FCSTD DOCUMENT  (FreeCAD 1.0R39109 (Git))
Label: SD7037 Airfoil Wing w Struts
License: All rights reserved
LicenseURL: https://en.wikipedia.org/wiki/All_rights_reserved
objects: Part::Part2DObjectPython×3, App::DocumentObjectGroup×1, Sketcher::SketchObject×1
note: 5 computed .brp shape members not serialized (recipe doc carries the construction recipe); baked Part::Feature solids carry a one-line shape summary decoded from their .brp

FEATURE [Part::Part2DObjectPython] Wire  # Draft 2D object (typed FeaturePython)
  Area = 0.0605284
  ChamferSize = 0
  Closed = true
  End = (1,0,0)
  FilletRadius = 0
  Length = 2.02979
  MakeFace = true
  Points = (61) [(1,0,0),(0.99672,0.00042,0),(0.98707,0.0018,0),(0.97146,0.00436,0),(0.95041,0.00811,0),(0.9245,0.01295,0),(0.89425,0.01865,0),(0.86015,0.0249,0),+53 more]
  Start = (1,0,0)
  Subdivisions = 0
FEATURE [App::DocumentObjectGroup] sd7037
  Group = -> [Wire]
FEATURE [Part::Part2DObjectPython] BSpline  # Draft 2D object (typed FeaturePython)
  Area = 0.0607194
  Closed = true
  MakeFace = true
  Parameterization = 1
  Points = (60) [(1,0,0),(0.99672,0.00042,0),(0.98707,0.0018,0),(0.97146,0.00436,0),(0.95041,0.00811,0),(0.9245,0.01295,0),(0.89425,0.01865,0),(0.86015,0.0249,0),+52 more]
FEATURE [Part::Part2DObjectPython] Wire001  # Draft 2D object (typed FeaturePython)
  Area = 0.0605284
  ChamferSize = 0
  Closed = true
  End = (0.99671,0.00021,0)
  FilletRadius = 0
  Length = 2.02979
  MakeFace = true
  Points = (60) [(1,0,0),(0.99672,0.00042,0),(0.98707,0.0018,0),(0.97146,0.00436,0),(0.95041,0.00811,0),(0.9245,0.01295,0),(0.89425,0.01865,0),(0.86015,0.0249,0),+52 more]
  Start = (1,0,0)
  Subdivisions = 0
FEATURE [Sketcher::SketchObject] Sketch
  ArcFitTolerance = 1e-06
  FullyConstrained = false
  MakeInternals = false
  sketch-geometry (210):
    g0: BSplineCurve PolesCount=61 KnotsCount=61 Degree=3 IsPeriodic=1
    g1-g61: Circle [constr] x61 (B-spline internal-alignment scaffolding for g0; pole/knot coordinates omitted)
    g62-g122: GeomPoint [constr] x61 (B-spline internal-alignment scaffolding for g0; pole/knot coordinates omitted)
    g123: LineSegment StartX=0.00694907 StartY=0.00753743 StartZ=0 EndX=0.0125619 EndY=0.0134873 EndZ=0
    g124: LineSegment StartX=0.0125619 StartY=0.0134873 StartZ=0 EndX=0.0195813 EndY=0.0193542 EndZ=0
    g125: LineSegment StartX=0.0195813 StartY=0.0193542 StartZ=0 EndX=0.0310295 EndY=0.0261498 EndZ=0
    g126: LineSegment StartX=0.0310295 StartY=0.0261498 StartZ=0 EndX=0.046426 EndY=0.033489 EndZ=0
    g127: LineSegment StartX=0.046426 StartY=0.033489 StartZ=0 EndX=0.063433 EndY=0.039816 EndZ=0
    g128: LineSegment StartX=0.063433 StartY=0.039816 StartZ=0 EndX=0.076674 EndY=0.044075 EndZ=0
    g129: LineSegment StartX=0.076674 StartY=0.044075 StartZ=0 EndX=0.093252 EndY=0.048694 EndZ=0
    g130: LineSegment StartX=0.093252 StartY=0.048694 StartZ=0 EndX=0.121289 EndY=0.055066 EndZ=0
    g131: LineSegment StartX=0.121289 StartY=0.055066 StartZ=0 EndX=0.15085 EndY=0.059941 EndZ=0
    g132: LineSegment StartX=0.15085 StartY=0.059941 StartZ=0 EndX=0.187176 EndY=0.064723 EndZ=0
    g133: LineSegment StartX=0.187176 StartY=0.064723 StartZ=0 EndX=0.221818 EndY=0.06734 EndZ=0
    g134: LineSegment StartX=0.221818 StartY=0.06734 StartZ=0 EndX=0.262808 EndY=0.069398 EndZ=0
    g135: LineSegment StartX=0.262808 StartY=0.069398 StartZ=0 EndX=0.305939 EndY=0.071198 EndZ=0
    g136: LineSegment StartX=0.305939 StartY=0.071198 StartZ=0 EndX=0.351804 EndY=0.071413 EndZ=0
    g137: LineSegment StartX=0.351804 StartY=0.071413 StartZ=0 EndX=0.399304 EndY=0.07049 EndZ=0
    g138: LineSegment StartX=0.399304 StartY=0.07049 StartZ=0 EndX=0.447775 EndY=0.068433 EndZ=0
    g139: LineSegment StartX=0.447775 StartY=0.068433 StartZ=0 EndX=0.497089 EndY=0.065532 EndZ=0
    g140: LineSegment StartX=0.497089 StartY=0.065532 StartZ=0 EndX=0.546658 EndY=0.061579 EndZ=0
    g141: LineSegment StartX=0.546658 StartY=0.061579 StartZ=0 EndX=0.596216 EndY=0.057292 EndZ=0
    g142: LineSegment StartX=0.596216 StartY=0.057292 StartZ=0 EndX=0.644863 EndY=0.0522 EndZ=0
    g143: LineSegment StartX=0.644863 StartY=0.0522 StartZ=0 EndX=0.692328 EndY=0.046604 EndZ=0
    g144: LineSegment StartX=0.692328 StartY=0.046604 StartZ=0 EndX=0.737563 EndY=0.040632 EndZ=0
    g145: LineSegment StartX=0.737563 StartY=0.040632 StartZ=0 EndX=0.781012 EndY=0.033957 EndZ=0
    g146: LineSegment StartX=0.781012 StartY=0.033957 StartZ=0 EndX=0.821267 EndY=0.027432 EndZ=0
    g147: LineSegment StartX=0.821267 StartY=0.027432 StartZ=0 EndX=0.858879 EndY=0.0213306 EndZ=0
    g148: LineSegment StartX=0.858879 StartY=0.0213306 StartZ=0 EndX=0.892665 EndY=0.0148511 EndZ=0
    g149: LineSegment StartX=0.892665 StartY=0.0148511 StartZ=0 EndX=0.922433 EndY=0.009352 EndZ=0
    g150: LineSegment StartX=0.922433 StartY=0.009352 StartZ=0 EndX=0.922433 EndY=0.005833 EndZ=0
    g151: LineSegment StartX=0.922433 StartY=0.005833 StartZ=0 EndX=0.918863 EndY=0.0059661 EndZ=0
    g152: LineSegment StartX=0.918863 StartY=0.0059661 StartZ=0 EndX=0.885982 EndY=0.00601026 EndZ=0
    g153: LineSegment StartX=0.885982 StartY=0.00601026 StartZ=0 EndX=0.848173 EndY=0.00560124 EndZ=0
    g154: LineSegment StartX=0.848173 StartY=0.00560124 StartZ=0 EndX=0.806229 EndY=0.004744 EndZ=0
    g155: LineSegment StartX=0.806229 StartY=0.004744 StartZ=0 EndX=0.76072 EndY=0.003693 EndZ=0
    g156: LineSegment StartX=0.76072 StartY=0.003693 StartZ=0 EndX=0.712179 EndY=0.002075 EndZ=0
    g157: LineSegment StartX=0.712179 StartY=0.002075 StartZ=0 EndX=0.661184 EndY=0.000677 EndZ=0
    g158: LineSegment StartX=0.661184 StartY=0.000677 StartZ=0 EndX=0.60857 EndY=-0.001721 EndZ=0
    g159: LineSegment StartX=0.60857 StartY=-0.001721 StartZ=0 EndX=0.554773 EndY=-0.003666 EndZ=0
    g160: LineSegment StartX=0.554773 StartY=-0.003666 StartZ=0 EndX=0.500583 EndY=-0.005865 EndZ=0
    g161: LineSegment StartX=0.500583 StartY=-0.005865 StartZ=0 EndX=0.446473 EndY=-0.008119 EndZ=0
    g162: LineSegment StartX=0.446473 StartY=-0.008119 StartZ=0 EndX=0.392927 EndY=-0.010205 EndZ=0
    g163: LineSegment StartX=0.392927 StartY=-0.010205 StartZ=0 EndX=0.341112 EndY=-0.012179 EndZ=0
    g164: LineSegment StartX=0.341112 StartY=-0.012179 StartZ=0 EndX=0.2915 EndY=-0.013654 EndZ=0
    g165: LineSegment StartX=0.2915 StartY=-0.013654 StartZ=0 EndX=0.243969 EndY=-0.015196 EndZ=0
    g166: LineSegment StartX=0.243969 StartY=-0.015196 StartZ=0 EndX=0.199561 EndY=-0.016029 EndZ=0
    g167: LineSegment StartX=0.199561 StartY=-0.016029 StartZ=0 EndX=0.158894 EndY=-0.016719 EndZ=0
    g168: LineSegment StartX=0.158894 StartY=-0.016719 StartZ=0 EndX=0.12214 EndY=-0.016719 EndZ=0
    g169: LineSegment StartX=0.12214 StartY=-0.016719 StartZ=0 EndX=0.09007 EndY=-0.015592 EndZ=0
    g170: LineSegment StartX=0.09007 StartY=-0.015592 StartZ=0 EndX=0.062735 EndY=-0.0141 EndZ=0
    g171: LineSegment StartX=0.062735 StartY=-0.0141 StartZ=0 EndX=0.040136 EndY=-0.012013 EndZ=0
    g172: LineSegment StartX=0.040136 StartY=-0.012013 StartZ=0 EndX=0.022408 EndY=-0.009222 EndZ=0
    g173: LineSegment StartX=0.022408 StartY=-0.009222 StartZ=0 EndX=0.011339 EndY=-0.005729 EndZ=0
    g174: LineSegment StartX=0.011339 StartY=-0.005729 StartZ=0 EndX=0.00795469 EndY=-0.00438723 EndZ=0
    g175: LineSegment StartX=0.00795469 StartY=-0.00438723 StartZ=0 EndX=0.00694907 EndY=0.00753743 EndZ=0
    g176: LineSegment StartX=0.909958 StartY=0.00597806 StartZ=0 EndX=0.906703 EndY=0.0121588 EndZ=0
    g177: LineSegment StartX=0.887466 StartY=0.00600827 StartZ=0 EndX=0.881703 EndY=0.0169534 EndZ=0
    g178: LineSegment StartX=0.857716 StartY=0.00570448 StartZ=0 EndX=0.846098 EndY=0.0237816 EndZ=0
    g179: LineSegment StartX=0.879484 StartY=0.00593996 StartZ=0 EndX=0.871098 EndY=0.0189871 EndZ=0
    g180: LineSegment StartX=0.843422 StartY=0.00550414 StartZ=0 EndX=0.832006 EndY=0.0256913 EndZ=0
    g181: LineSegment StartX=0.820973 StartY=0.00504533 StartZ=0 EndX=0.807006 EndY=0.0297436 EndZ=0
    g182: LineSegment StartX=0.782636 StartY=0.00419913 StartZ=0 EndX=0.781012 EndY=0.033957 EndZ=0
    g183: LineSegment StartX=0.757878 StartY=0.00359827 StartZ=0 EndX=0.756012 EndY=0.0377977 EndZ=0
    g184: LineSegment StartX=0.729719 StartY=0.00265965 StartZ=0 EndX=0.705034 EndY=0.0449265 EndZ=0
    g185: LineSegment StartX=0.70697 StartY=0.0019322 StartZ=0 EndX=0.680034 EndY=0.0480534 EndZ=0
    g186: LineSegment StartX=0.66105 StartY=0.000670909 StartZ=0 EndX=0.674658 EndY=0.0486872 EndZ=0
    g187: LineSegment StartX=0.634877 StartY=-0.000522 StartZ=0 EndX=0.649658 EndY=0.0516347 EndZ=0
    g188: LineSegment StartX=0.616032 StartY=-0.0013809 StartZ=0 EndX=0.586217 EndY=0.058157 EndZ=0
    g189: LineSegment StartX=0.592575 StartY=-0.00229929 StartZ=0 EndX=0.561217 EndY=0.0603196 EndZ=0
    g190: LineSegment StartX=0.546874 StartY=0.0615618 StartZ=0 EndX=0.52413 EndY=-0.00490949 EndZ=0
    g191: LineSegment StartX=0.521873 StartY=0.0635555 StartZ=0 EndX=0.498085 EndY=-0.00596906 EndZ=0
    g192: LineSegment StartX=0.48301 StartY=-0.00659701 StartZ=0 EndX=0.445099 EndY=0.0685466 EndZ=0
    g193: LineSegment StartX=0.459049 StartY=-0.00759514 StartZ=0 EndX=0.420099 EndY=0.0696075 EndZ=0
    g194: LineSegment StartX=0.414592 StartY=0.0698412 StartZ=0 EndX=0.395122 EndY=-0.0101214 EndZ=0
    g195: LineSegment StartX=0.389592 StartY=0.0706787 StartZ=0 EndX=0.369682 EndY=-0.0110906 EndZ=0
    g196: LineSegment StartX=0.350859 StartY=-0.0118077 StartZ=0 EndX=0.313001 EndY=0.0712311 EndZ=0
    g197: LineSegment StartX=0.325878 StartY=-0.0126319 StartZ=0 EndX=0.288001 EndY=0.0704494 EndZ=0
    g198: LineSegment StartX=0.269666 StartY=0.0696842 StartZ=0 EndX=0.249799 EndY=-0.0150069 EndZ=0
    g199: LineSegment StartX=0.244666 StartY=0.0686409 StartZ=0 EndX=0.227935 EndY=-0.0157162 EndZ=0
    g200: LineSegment StartX=0.219718 StartY=-0.0156509 StartZ=0 EndX=0.17404 EndY=0.0637307 EndZ=0
    g201: LineSegment StartX=0.204912 StartY=-0.0159286 StartZ=0 EndX=0.14904 EndY=0.0618421 EndZ=0
    g202: LineSegment StartX=0.169013 StartY=0.062332 StartZ=0 EndX=0.150125 EndY=-0.016719 EndZ=0
    g203: LineSegment StartX=0.144013 StartY=0.059041 StartZ=0 EndX=0.136509 EndY=-0.016719 EndZ=0
    g204: LineSegment StartX=0.119208 StartY=-0.016616 StartZ=0 EndX=0.106403 EndY=0.0523582 EndZ=0
    g205: LineSegment StartX=0.106105 StartY=-0.0161555 StartZ=0 EndX=0.081403 EndY=0.0453926 EndZ=0
    g206: LineSegment StartX=0.068635 StartY=0.0414892 StartZ=0 EndX=0.048492 EndY=-0.0127847 EndZ=0
    g207: LineSegment StartX=0.0417254 StartY=0.0317403 StartZ=0 EndX=0.034761 EndY=-0.0111668 EndZ=0
    g208: LineSegment StartX=0.025995 StartY=-0.00978672 StartZ=0 EndX=0.013534 EndY=0.0142998 EndZ=0
    g209: LineSegment StartX=0.016004 StartY=-0.00720112 StartZ=0 EndX=0.00768826 EndY=0.008321 EndZ=0
  constraints (325):
    c: InternalAlignment(g1,g0)
    c: Weight(g1) = 1
    c: InternalAlignment(g2,g0)
    c: Equal(g2,g1)
    c: InternalAlignment(g3,g0)
    c: Equal(g3,g1)
    c: InternalAlignment(g4,g0)
    c: Equal(g4,g1)
    c: InternalAlignment(g5,g0)
    c: Equal(g5,g1)
    c: InternalAlignment(g6,g0)
    c: Equal(g6,g1)
    c: InternalAlignment(g7,g0)
    c: Equal(g7,g1)
    c: InternalAlignment(g8,g0)
    c: Equal(g8,g1)
    c: InternalAlignment(g9,g0)
    c: Equal(g9,g1)
    c: InternalAlignment(g10,g0)
    c: Equal(g10,g1)
    c: InternalAlignment(g11,g0)
    c: Equal(g11,g1)
    c: InternalAlignment(g12,g0)
    c: Equal(g12,g1)
    c: InternalAlignment(g13,g0)
    c: Equal(g13,g1)
    c: InternalAlignment(g14,g0)
    c: Equal(g14,g1)
    c: InternalAlignment(g15,g0)
    c: Equal(g15,g1)
    c: InternalAlignment(g16,g0)
    c: Equal(g16,g1)
    c: InternalAlignment(g17,g0)
    c: Equal(g17,g1)
    c: InternalAlignment(g18,g0)
    c: Equal(g18,g1)
    c: InternalAlignment(g19,g0)
    c: Equal(g19,g1)
    c: InternalAlignment(g20,g0)
    c: Equal(g20,g1)
    c: InternalAlignment(g21,g0)
    c: Equal(g21,g1)
    c: InternalAlignment(g22,g0)
    c: Equal(g22,g1)
    c: InternalAlignment(g23,g0)
    c: Equal(g23,g1)
    c: InternalAlignment(g24,g0)
    c: Equal(g24,g1)
    c: InternalAlignment(g25,g0)
    c: Equal(g25,g1)
    c: InternalAlignment(g26,g0)
    c: Equal(g26,g1)
    c: InternalAlignment(g27,g0)
    c: Equal(g27,g1)
    c: InternalAlignment(g28,g0)
    c: Equal(g28,g1)
    c: InternalAlignment(g29,g0)
    c: Equal(g29,g1)
    c: InternalAlignment(g30,g0)
    c: Equal(g30,g1)
    c: InternalAlignment(g31,g0)
    c: Equal(g31,g1)
    c: InternalAlignment(g32,g0)
    c: Equal(g32,g1)
    c: InternalAlignment(g33,g0)
    c: Equal(g33,g1)
    c: InternalAlignment(g34,g0)
    c: Equal(g34,g1)
    c: InternalAlignment(g35,g0)
    c: Equal(g35,g1)
    c: InternalAlignment(g36,g0)
    c: Equal(g36,g1)
    c: InternalAlignment(g37,g0)
    c: Equal(g37,g1)
    c: InternalAlignment(g38,g0)
    c: Equal(g38,g1)
    c: InternalAlignment(g39,g0)
    c: Equal(g39,g1)
    c: InternalAlignment(g40,g0)
    c: Equal(g40,g1)
    c: InternalAlignment(g41,g0)
    c: Equal(g41,g1)
    c: InternalAlignment(g42,g0)
    c: Equal(g42,g1)
    c: InternalAlignment(g43,g0)
    c: Equal(g43,g1)
    c: InternalAlignment(g44,g0)
    c: Equal(g44,g1)
    c: InternalAlignment(g45,g0)
    c: Equal(g45,g1)
    c: InternalAlignment(g46,g0)
    c: Equal(g46,g1)
    c: InternalAlignment(g47,g0)
    c: Equal(g47,g1)
    c: InternalAlignment(g48,g0)
    c: Equal(g48,g1)
    c: InternalAlignment(g49,g0)
    c: Equal(g49,g1)
    c: InternalAlignment(g50,g0)
    c: Equal(g50,g1)
    c: InternalAlignment(g51,g0)
    c: Equal(g51,g1)
    c: InternalAlignment(g52,g0)
    c: Equal(g52,g1)
    c: InternalAlignment(g53,g0)
    c: Equal(g53,g1)
    c: InternalAlignment(g54,g0)
    c: Equal(g54,g1)
    c: InternalAlignment(g55,g0)
    c: Equal(g55,g1)
    c: InternalAlignment(g56,g0)
    c: Equal(g56,g1)
    c: InternalAlignment(g57,g0)
    c: Equal(g57,g1)
    c: InternalAlignment(g58,g0)
    c: Equal(g58,g1)
    c: InternalAlignment(g59,g0)
    c: Equal(g59,g1)
    c: InternalAlignment(g60,g0)
    c: Equal(g60,g1)
    c: InternalAlignment(g61,g0)
    c: Equal(g61,g1)
    c: InternalAlignment(g62-g122 -> g0) x61
    c: Coincident(g123,g124)
    c: Coincident(g124,g125)
    c: Coincident(g125,g126)
    c: Coincident(g126,g127)
    c: Coincident(g127,g128)
    c: Coincident(g128,g129)
    c: Coincident(g129,g130)
    c: Coincident(g130,g131)
    c: Coincident(g131,g132)
    c: Coincident(g132,g133)
    c: Coincident(g133,g134)
    c: Coincident(g134,g135)
    c: Coincident(g135,g136)
    c: Coincident(g136,g137)
    c: Coincident(g137,g138)
    c: Coincident(g138,g139)
    c: Coincident(g139,g140)
    c: Coincident(g140,g141)
    c: Coincident(g141,g142)
    c: Coincident(g142,g143)
    c: Coincident(g143,g144)
    c: Coincident(g144,g145)
    c: Coincident(g145,g146)
    c: Coincident(g146,g147)
    c: Coincident(g147,g148)
    c: Coincident(g148,g149)
    c: Coincident(g149,g150)
    c: Vertical(g150)
    c: Coincident(g150,g151)
    c: Coincident(g151,g152)
    c: Coincident(g152,g153)
    c: Coincident(g153,g154)
    c: Coincident(g154,g155)
    c: Coincident(g155,g156)
    c: Coincident(g156,g157)
    c: Coincident(g157,g158)
    c: Coincident(g158,g159)
    c: Coincident(g159,g160)
    c: Coincident(g160,g161)
    c: Coincident(g161,g162)
    c: Coincident(g162,g163)
    c: Coincident(g163,g164)
    c: Coincident(g164,g165)
    c: Coincident(g165,g166)
    c: Coincident(g166,g167)
    c: Coincident(g167,g168)
    c: Horizontal(g168)
    c: Coincident(g168,g169)
    c: Coincident(g169,g170)
    c: Coincident(g170,g171)
    c: Coincident(g171,g172)
    c: Coincident(g172,g173)
    c: Coincident(g173,g174)
    c: Coincident(g174,g175)
    c: Coincident(g175,g123)
    c: PointOnObject(g176,g152)
    c: PointOnObject(g176,g148)
    c: PointOnObject(g177,g152)
    c: PointOnObject(g177,g148)
    c: Parallel(g177,g176)
    c: PointOnObject(g178,g153)
    c: PointOnObject(g178,g148)
    c: PointOnObject(g179,g153)
    c: PointOnObject(g179,g148)
    c: Parallel(g178,g179)
    c: Block(g147)
    c: Block(g124)
    c: Block(g123)
    c: Block(g175)
    c: Block(g174)
    c: Block(g173)
    c: Block(g172)
    c: Block(g171)
    c: Block(g170)
    c: Block(g169)
    c: Block(g168)
    c: Block(g167)
    c: Block(g166)
    c: Block(g165)
    c: Block(g164)
    c: Block(g163)
    c: Block(g162)
    c: Block(g161)
    c: Block(g160)
    c: Block(g159)
    c: Block(g158)
    c: Block(g157)
    c: Block(g156)
    c: Block(g155)
    c: Block(g154)
    c: Block(g153)
    c: Block(g152)
    c: Block(g150)
    c: Block(g149)
    c: Block(g148)
    c: Block(g146)
    c: Block(g145)
    c: Block(g144)
    c: Block(g143)
    c: Block(g142)
    c: Block(g141)
    c: Block(g140)
    c: Block(g139)
    c: Block(g138)
    c: Block(g137)
    c: Block(g136)
    c: Block(g135)
    c: Block(g134)
    c: Block(g133)
    c: Block(g132)
    c: Block(g131)
    c: Block(g130)
    c: Block(g129)
    c: Block(g128)
    c: Block(g127)
    c: Block(g126)
    c: Block(g125)
    c: PointOnObject(g180,g154)
    c: PointOnObject(g180,g146)
    c: PointOnObject(g181,g154)
    c: PointOnObject(g181,g146)
    c: PointOnObject(g182,g155)
    c: Coincident(g182,g145)
    c: PointOnObject(g183,g156)
    c: PointOnObject(g183,g145)
    c: PointOnObject(g184,g156)
    c: PointOnObject(g184,g144)
    c: PointOnObject(g185,g157)
    c: PointOnObject(g185,g143)
    c: PointOnObject(g186,g158)
    c: PointOnObject(g186,g143)
    c: Symmetric(g158,g158,g187)
    c: PointOnObject(g187,g143)
    c: PointOnObject(g188,g158)
    c: PointOnObject(g188,g141)
    c: PointOnObject(g189,g159)
    c: PointOnObject(g189,g141)
    c: PointOnObject(g190,g140)
    c: PointOnObject(g190,g160)
    c: Symmetric(g140,g140,g191)
    c: PointOnObject(g191,g161)
    c: PointOnObject(g192,g161)
    c: PointOnObject(g192,g138)
    c: PointOnObject(g193,g161)
    c: PointOnObject(g193,g138)
    c: PointOnObject(g194,g138)
    c: PointOnObject(g194,g163)
    c: PointOnObject(g195,g137)
    c: PointOnObject(g195,g163)
    c: PointOnObject(g196,g163)
    c: PointOnObject(g196,g136)
    c: PointOnObject(g197,g164)
    c: PointOnObject(g197,g135)
    c: PointOnObject(g198,g135)
    c: PointOnObject(g198,g165)
    c: PointOnObject(g199,g135)
    c: PointOnObject(g199,g165)
    c: PointOnObject(g200,g166)
    c: PointOnObject(g200,g133)
    c: PointOnObject(g201,g166)
    c: PointOnObject(g201,g133)
    c: Symmetric(g132,g132,g202)
    c: PointOnObject(g202,g168)
    c: PointOnObject(g203,g132)
    c: PointOnObject(g203,g168)
    c: PointOnObject(g204,g169)
    c: PointOnObject(g204,g129)
    c: Symmetric(g169,g169,g205)
    c: PointOnObject(g205,g129)
    c: PointOnObject(g206,g128)
    c: PointOnObject(g206,g171)
    c: PointOnObject(g207,g127)
    c: PointOnObject(g207,g172)
    c: PointOnObject(g208,g172)
    c: PointOnObject(g208,g124)
    c: PointOnObject(g209,g173)
    c: PointOnObject(g209,g123)
    c: DistanceX(g177,g176) = 0.025
    c: DistanceX(g178,g179) = 0.025
    c: DistanceX(g181,g180) = 0.025
    c: DistanceX(g183,g145) = 0.025
    c: DistanceX(g185,g184) = 0.025
    c: DistanceX(g187,g186) = 0.025
    c: DistanceX(g189,g188) = 0.025
    c: DistanceX(g191,g190) = 0.025
    c: DistanceX(g193,g192) = 0.025
    c: DistanceX(g195,g194) = 0.025
    c: DistanceX(g197,g196) = 0.025
    c: DistanceX(g199,g198) = 0.025
    c: DistanceX(g201,g200) = 0.025
    c: DistanceX(g203,g202) = 0.025
    c: DistanceX(g205,g204) = 0.025
    c: Distance(g206,g207) = 0.025
    c: Parallel(g181,g180)
    c: Parallel(g182,g183)
    c: Parallel(g184,g185)
    c: Parallel(g187,g186)
    c: Parallel(g188,g189)
    c: Parallel(g190,g191)
    c: Parallel(g192,g193)
    c: Parallel(g195,g194)
    c: Parallel(g196,g197)
